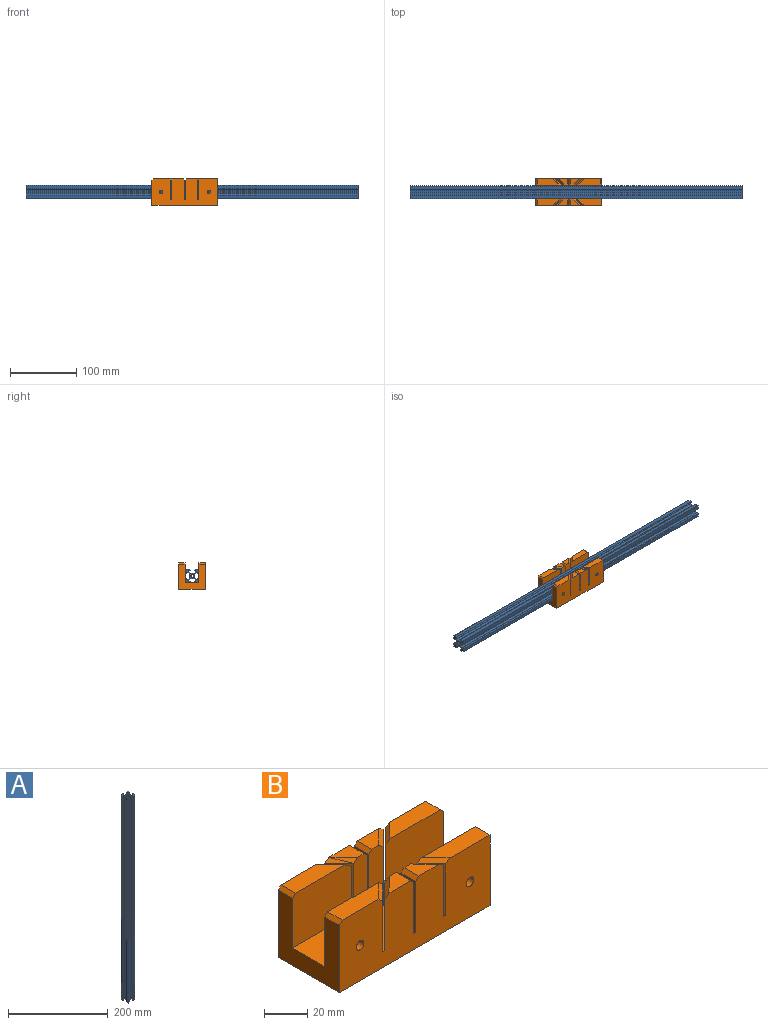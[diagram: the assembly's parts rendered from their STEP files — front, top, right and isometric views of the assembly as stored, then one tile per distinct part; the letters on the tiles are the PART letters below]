
ASSEMBLY  parts=2 mates=2
PART A: 71 faces, bbox 20x20x500 mm
  f0: plane 500x0.21mm, normal (0.71,-0.71,0), area 148.5mm2, adj f1,f67,f68,f69
  f1: plane 500x2.63mm, normal (1,0,0), area 1314.7mm2, adj f0,f2,f68,f69
  f2: plane 500x2.66mm, normal (0.71,-0.71,0), area 1881.4mm2, adj f1,f3,f68,f69
  f3: plane 500x1.64mm, normal (0,-1,0), area 819.7mm2, adj f2,f4,f68,f69
  f4: plane 500x2.38mm, normal (-1,0,0), area 1187.5mm2, adj f3,f5,f68,f69
  f5: plane 500x0.35mm, normal (0,-1,0), area 172.5mm2, adj f4,f6,f68,f69
  f6: plane 500x1.46mm, normal (0.71,-0.71,0), area 1028.8mm2, adj f5,f7,f68,f69
  f7: plane 500x4.92mm, normal (1,0,0), area 2460mm2, adj f6,f8,f68,f69
  f8: cylinder r=0.5mm len=500mm, axis (0,0,-1), area 392.7mm2, adj f7,f9,f68,f69
  f9: plane 500x4.92mm, normal (0,1,0), area 2460mm2, adj f8,f10,f68,f69
  f10: plane 500x1.46mm, normal (-0.71,0.71,0), area 1028.8mm2, adj f9,f11,f68,f69
  f11: plane 500x0.35mm, normal (-1,0,0), area 172.5mm2, adj f10,f12,f68,f69
  f12: plane 500x2.38mm, normal (0,-1,0), area 1187.5mm2, adj f11,f13,f68,f69
  f13: plane 500x1.64mm, normal (-1,0,0), area 819.7mm2, adj f12,f14,f68,f69
  f14: plane 500x2.66mm, normal (-0.71,0.71,0), area 1881.4mm2, adj f13,f15,f68,f69
  f15: plane 500x2.63mm, normal (0,1,0), area 1314.7mm2, adj f14,f16,f68,f69
  f16: plane 500x0.21mm, normal (-0.71,0.71,0), area 148.5mm2, adj f15,f17,f68,f69
  f17: plane 500x0.21mm, normal (0.71,0.71,0), area 148.5mm2, adj f16,f18,f68,f69
  f18: plane 500x2.63mm, normal (0,1,0), area 1314.7mm2, adj f17,f19,f68,f69
  f19: plane 500x2.66mm, normal (0.71,0.71,0), area 1881.4mm2, adj f18,f20,f68,f69
  f20: plane 500x1.64mm, normal (1,0,0), area 819.7mm2, adj f19,f21,f68,f69
  f21: plane 500x2.38mm, normal (0,-1,0), area 1187.5mm2, adj f20,f22,f68,f69
  f22: plane 500x0.35mm, normal (1,0,0), area 172.5mm2, adj f21,f23,f68,f69
  f23: plane 500x1.46mm, normal (0.71,0.71,0), area 1028.8mm2, adj f22,f24,f68,f69
  f24: plane 500x4.92mm, normal (0,1,0), area 2460mm2, adj f23,f25,f68,f69
  f25: cylinder r=0.5mm len=500mm, axis (0,0,-1), area 392.7mm2, adj f24,f26,f68,f69
  f26: plane 500x4.92mm, normal (-1,0,0), area 2460mm2, adj f25,f27,f68,f69
  f27: plane 500x1.46mm, normal (-0.71,-0.71,0), area 1028.8mm2, adj f26,f28,f68,f69
  f28: plane 500x0.35mm, normal (0,-1,0), area 172.5mm2, adj f27,f29,f68,f69
  f29: plane 500x2.38mm, normal (1,0,0), area 1187.5mm2, adj f28,f30,f68,f69
  f30: plane 500x1.64mm, normal (0,-1,0), area 819.7mm2, adj f29,f31,f68,f69
  f31: plane 500x2.66mm, normal (-0.71,-0.71,0), area 1881.4mm2, adj f30,f32,f68,f69
  f32: plane 500x2.63mm, normal (-1,0,0), area 1314.7mm2, adj f31,f33,f68,f69
  f33: plane 500x0.21mm, normal (-0.71,-0.71,0), area 148.5mm2, adj f32,f34,f68,f69
  f34: plane 500x0.21mm, normal (-0.71,0.71,0), area 148.5mm2, adj f33,f35,f68,f69
  f35: plane 500x2.63mm, normal (-1,0,0), area 1314.7mm2, adj f34,f36,f68,f69
  f36: plane 500x2.66mm, normal (-0.71,0.71,0), area 1881.4mm2, adj f35,f37,f68,f69
  f37: plane 500x1.64mm, normal (0,1,0), area 819.7mm2, adj f36,f38,f68,f69
  f38: plane 500x2.38mm, normal (1,0,0), area 1187.5mm2, adj f37,f39,f68,f69
  f39: plane 500x0.35mm, normal (0,1,0), area 172.5mm2, adj f38,f40,f68,f69
  f40: plane 500x1.46mm, normal (-0.71,0.71,0), area 1028.8mm2, adj f39,f41,f68,f69
  f41: plane 500x4.92mm, normal (-1,0,0), area 2460mm2, adj f40,f42,f68,f69
  f42: cylinder r=0.5mm len=500mm, axis (0,0,-1), area 392.7mm2, adj f41,f43,f68,f69
  f43: plane 500x4.92mm, normal (0,-1,0), area 2460mm2, adj f42,f44,f68,f69
  f44: plane 500x1.46mm, normal (0.71,-0.71,0), area 1028.8mm2, adj f43,f45,f68,f69
  f45: plane 500x0.35mm, normal (1,0,0), area 172.5mm2, adj f44,f46,f68,f69
  f46: plane 500x2.38mm, normal (0,1,0), area 1187.5mm2, adj f45,f47,f68,f69
  f47: plane 500x1.64mm, normal (1,0,0), area 819.7mm2, adj f46,f48,f68,f69
  f48: plane 500x2.66mm, normal (0.71,-0.71,0), area 1881.4mm2, adj f47,f49,f68,f69
  f49: plane 500x2.63mm, normal (0,-1,0), area 1314.7mm2, adj f48,f50,f68,f69
  f50: plane 500x0.21mm, normal (0.71,-0.71,0), area 148.5mm2, adj f49,f51,f68,f69
  f51: plane 500x0.21mm, normal (-0.71,-0.71,0), area 148.5mm2, adj f50,f52,f68,f69
  f52: plane 500x2.63mm, normal (0,-1,0), area 1314.7mm2, adj f51,f53,f68,f69
  f53: plane 500x2.66mm, normal (-0.71,-0.71,0), area 1881.4mm2, adj f52,f54,f68,f69
  f54: plane 500x1.64mm, normal (-1,0,0), area 819.7mm2, adj f53,f55,f68,f69
  f55: plane 500x2.38mm, normal (0,1,0), area 1187.5mm2, adj f54,f56,f68,f69
  f56: plane 500x0.35mm, normal (-1,0,0), area 172.5mm2, adj f55,f57,f68,f69
  f57: plane 500x1.46mm, normal (-0.71,-0.71,0), area 1028.8mm2, adj f56,f58,f68,f69
  f58: plane 500x4.92mm, normal (0,-1,0), area 2460mm2, adj f57,f59,f68,f69
  f59: cylinder r=0.5mm len=500mm, axis (0,0,-1), area 392.7mm2, adj f58,f60,f68,f69
  f60: plane 500x4.92mm, normal (1,0,0), area 2460mm2, adj f59,f61,f68,f69
  f61: plane 500x1.46mm, normal (0.71,0.71,0), area 1028.8mm2, adj f60,f62,f68,f69
  f62: plane 500x0.35mm, normal (0,1,0), area 172.5mm2, adj f61,f63,f68,f69
  f63: plane 500x2.38mm, normal (-1,0,0), area 1187.5mm2, adj f62,f64,f68,f69
  f64: plane 500x1.64mm, normal (0,1,0), area 819.7mm2, adj f63,f65,f68,f69
  f65: plane 500x2.66mm, normal (0.71,0.71,0), area 1881.4mm2, adj f64,f66,f68,f69
  f66: plane 500x2.63mm, normal (1,0,0), area 1314.7mm2, adj f65,f67,f68,f69
  f67: plane 500x0.21mm, normal (0.71,0.71,0), area 148.5mm2, adj f0,f66,f68,f69
  f68: plane 20x20mm, normal (0,0,1), area 171.4mm2, adj f0,f1,f2,f3,f4,f5,f6,f7
  f69: plane 20x20mm, normal (0,0,-1), area 171.4mm2, adj f0,f1,f2,f3,f4,f5,f6,f7
  f70: cylinder r=2.1mm len=500mm, axis (0,0,-1), area 6597.3mm2, adj f68,f69
PART B: 75 faces, bbox 98.5x40x40 mm
  f0: plane 98.5x40mm, normal (0,1,0), area 3798.8mm2, adj f2,f9,f10,f30,f31,f32,f34,f36
  f1: plane 98.5x40mm, normal (0,-1,0), area 3764.5mm2, adj f2,f3,f10,f41,f42,f43,f48,f49
  f2: plane 98.5x40mm, normal (0,0,-1), area 3939.8mm2, adj f0,f1,f59,f62
  f3: plane 13.63x9.5mm, normal (0,0,1), area 85.2mm2, adj f1,f4,f57,f63
  f4: plane 30x9.11mm, normal (0,1,0), area 268.4mm2, adj f3,f15,f54,f57,f63,f68
  f5: plane 9.3x9.29mm, normal (0,0,1), area 43.2mm2, adj f6,f8,f53
  f6: plane 9.3x9.29mm, normal (0.71,-0.71,0), area 6.6mm2, adj f5,f7,f53
  f7: plane 18.81x18.79mm, normal (0.71,-0.71,0), area 13.3mm2, adj f6,f10,f58
  f8: plane 30x9.3mm, normal (0,-1,0), area 274.3mm2, adj f5,f9,f53,f55,f56,f58
  f9: plane 13.98x9.5mm, normal (0,0,1), area 87.7mm2, adj f0,f8,f55,f56
  f10: plane 41.85x40mm, normal (0,0,1), area 150mm2, adj f0,f1,f7,f11,f14,f17,f20,f21
  f11: plane 20.03x20mm, normal (-0.71,0.71,0), area 14.2mm2, adj f10,f12,f66
  f12: plane 10.52x10.5mm, normal (-0.71,0.71,0), area 7.4mm2, adj f11,f13,f45
  f13: plane 10.5x10.31mm, normal (-0.71,-0.7,0), area 7.4mm2, adj f12,f14,f45
  f14: plane 20x19.63mm, normal (-0.71,-0.7,0), area 14mm2, adj f10,f13,f67
  f15: plane 9.28x9.11mm, normal (0,0,1), area 42.2mm2, adj f4,f16,f54
  f16: plane 9.28x9.11mm, normal (0.71,0.7,0), area 6.5mm2, adj f15,f17,f54
  f17: plane 18.78x18.44mm, normal (0.71,0.7,0), area 13.2mm2, adj f10,f16,f68
  f18: plane 9.5x9.31mm, normal (0,0,1), area 44.2mm2, adj f19,f41,f52
  f19: plane 9.5x9.31mm, normal (-0.7,0.71,0), area 6.6mm2, adj f18,f20,f41
  f20: plane 19.19x18.81mm, normal (-0.7,0.71,0), area 13.4mm2, adj f10,f19,f71
  f21: plane 19.99x19.6mm, normal (0.71,0.7,0), area 14mm2, adj f10,f22,f46
  f22: plane 10.49x10.29mm, normal (0.71,0.7,0), area 7.3mm2, adj f21,f23,f44
  f23: plane 10.72x10.51mm, normal (0.7,-0.71,0), area 7.5mm2, adj f22,f24,f44
  f24: plane 20.41x20.01mm, normal (0.7,-0.71,0), area 14.3mm2, adj f10,f23,f72
  f25: plane 9.28x9.09mm, normal (-0.71,-0.7,0), area 6.5mm2, adj f26,f27,f40
  f26: plane 9.28x9.09mm, normal (0,0,1), area 42.2mm2, adj f25,f28,f40
  f27: plane 18.78x18.4mm, normal (-0.71,-0.7,0), area 13.1mm2, adj f10,f25,f39
  f28: plane 30x9.09mm, normal (0,-1,0), area 268mm2, adj f26,f29,f31,f38,f39,f40
  f29: plane 9.5x9.31mm, normal (-0.5,-0.49,0.71), area 18.8mm2, adj f28,f30,f31
  f30: plane 9.5x9.31mm, normal (-0.51,-0.49,0.71), area 18.8mm2, adj f0,f29,f39
  f31: plane 13.6x9.5mm, normal (0,0,1), area 85mm2, adj f0,f28,f29,f38
  f32: plane 9.5x9.31mm, normal (0.51,0.49,0.71), area 28.2mm2, adj f0,f33,f34
  f33: plane 9.5x9.31mm, normal (0.5,0.49,0.71), area 28.2mm2, adj f32,f35,f46
  f34: plane 32.1x9.5mm, normal (0,0,1), area 260.8mm2, adj f0,f32,f35,f61
  f35: plane 38.3x30mm, normal (0,-1,0), area 1140.8mm2, adj f33,f34,f44,f46,f61,f62
  f36: plane 33.15x9.5mm, normal (0,0,1), area 269.8mm2, adj f0,f37,f64,f65
  f37: plane 37.98x30mm, normal (0,-1,0), area 1134.6mm2, adj f36,f45,f59,f64,f65,f66
  f38: plane 9.5x2mm, normal (0.71,0,0.71), area 26.9mm2, adj f0,f28,f31,f40
  f39: plane 29x9.5mm, normal (-0.71,-0.7,0), area 379.1mm2, adj f0,f27,f28,f30
  f40: plane 29x18.78mm, normal (1,0,0), area 284.8mm2, adj f0,f10,f25,f26,f28,f38
  f41: plane 29x18.81mm, normal (1,0,0), area 284.8mm2, adj f1,f10,f18,f19,f43,f52
  f42: plane 14.33x9.5mm, normal (0,0,1), area 90.1mm2, adj f1,f43,f52,f69
  f43: plane 9.5x2mm, normal (0.71,0,0.71), area 26.9mm2, adj f1,f41,f42,f52
  f44: plane 48.59x21mm, normal (0,0,1), area 910.1mm2, adj f22,f23,f35,f50,f62
  f45: plane 48.5x21mm, normal (0,0,1), area 909.1mm2, adj f12,f13,f37,f47,f59
  f46: plane 28x9.5mm, normal (0.71,0.7,0), area 365.8mm2, adj f0,f21,f33,f35
  f47: plane 38.19x30mm, normal (0,1,0), area 1123.3mm2, adj f45,f48,f49,f59,f67,f74
  f48: plane 12.13x9.5mm, normal (-0.5,-0.5,0.71), area 37.7mm2, adj f1,f47,f49,f67
  f49: plane 35.39x9.5mm, normal (0,0,1), area 291.9mm2, adj f1,f47,f48,f59
  f50: plane 37.87x30mm, normal (0,1,0), area 1111.6mm2, adj f44,f51,f60,f62,f70,f72,f73
  f51: plane 33.01x9.5mm, normal (0,0,1), area 267.6mm2, adj f1,f50,f60,f70
  f52: plane 30x9.5mm, normal (0,1,0), area 280.1mm2, adj f18,f41,f42,f43,f69,f71
  f53: plane 29x18.79mm, normal (-1,0,0), area 284.8mm2, adj f0,f5,f6,f8,f10,f56
  f54: plane 29x18.78mm, normal (-1,0,0), area 284.8mm2, adj f1,f4,f10,f15,f16,f57
  f55: plane 12.34x9.5mm, normal (0.5,-0.5,0.71), area 38mm2, adj f0,f8,f9,f58
  f56: plane 9.5x2mm, normal (-0.71,0,0.71), area 26.9mm2, adj f0,f8,f9,f53
  f57: plane 9.5x2mm, normal (-0.71,0,0.71), area 26.9mm2, adj f1,f3,f4,f54
  f58: plane 29x9.51mm, normal (0.71,-0.71,0), area 383.1mm2, adj f0,f7,f8,f55
  f59: plane 40x40mm, normal (1,0,0), area 951mm2, adj f0,f1,f2,f37,f45,f47,f49,f65
  f60: plane 9.5x2mm, normal (-0.71,0,0.71), area 26.9mm2, adj f1,f50,f51,f62
  f61: plane 9.5x2mm, normal (-0.71,0,0.71), area 26.9mm2, adj f0,f34,f35,f62
  f62: plane 40x38mm, normal (-1,0,0), area 932mm2, adj f0,f1,f2,f35,f44,f50,f60,f61
  f63: plane 12.13x9.5mm, normal (0.5,0.5,0.71), area 37.7mm2, adj f1,f3,f4,f68
  f64: plane 12.34x9.5mm, normal (-0.5,0.5,0.71), area 38mm2, adj f0,f36,f37,f66
  f65: plane 9.5x2mm, normal (0.71,0,0.71), area 26.9mm2, adj f0,f36,f37,f59
  f66: plane 29x9.51mm, normal (-0.71,0.71,0), area 383.1mm2, adj f0,f11,f37,f64
  f67: plane 29x9.5mm, normal (-0.71,-0.7,0), area 379.4mm2, adj f1,f14,f47,f48
  f68: plane 29x9.5mm, normal (0.71,0.7,0), area 379.4mm2, adj f1,f4,f17,f63
  f69: plane 12.55x9.5mm, normal (-0.49,0.5,0.71), area 38.4mm2, adj f1,f42,f52,f71
  f70: plane 12.55x9.5mm, normal (0.49,-0.5,0.71), area 38.4mm2, adj f1,f50,f51,f72
  f71: plane 29x9.69mm, normal (-0.7,0.71,0), area 386.8mm2, adj f1,f20,f52,f69
  f72: plane 29x9.69mm, normal (0.7,-0.71,0), area 386.8mm2, adj f1,f24,f50,f70
  f73: cylinder r=2.5mm len=9.5mm, axis (0,-1,0), area 149.2mm2, adj f1,f50
  f74: cylinder r=2.5mm len=9.5mm, axis (0,-1,0), area 149.2mm2, adj f1,f47
PLACE A rot(axis=(0,-1,0),90deg) t=(261.01,-0.5,17.04)mm
PLACE B t=(0,0,-2.96)mm
MATE planar A.f41 <-> B.f45  axis (0,0,-1) through (11.01,-7.54,7.04)mm
MATE planar A.f43 <-> B.f47  axis (0,-1,0) through (11.01,-10.5,10)mm
